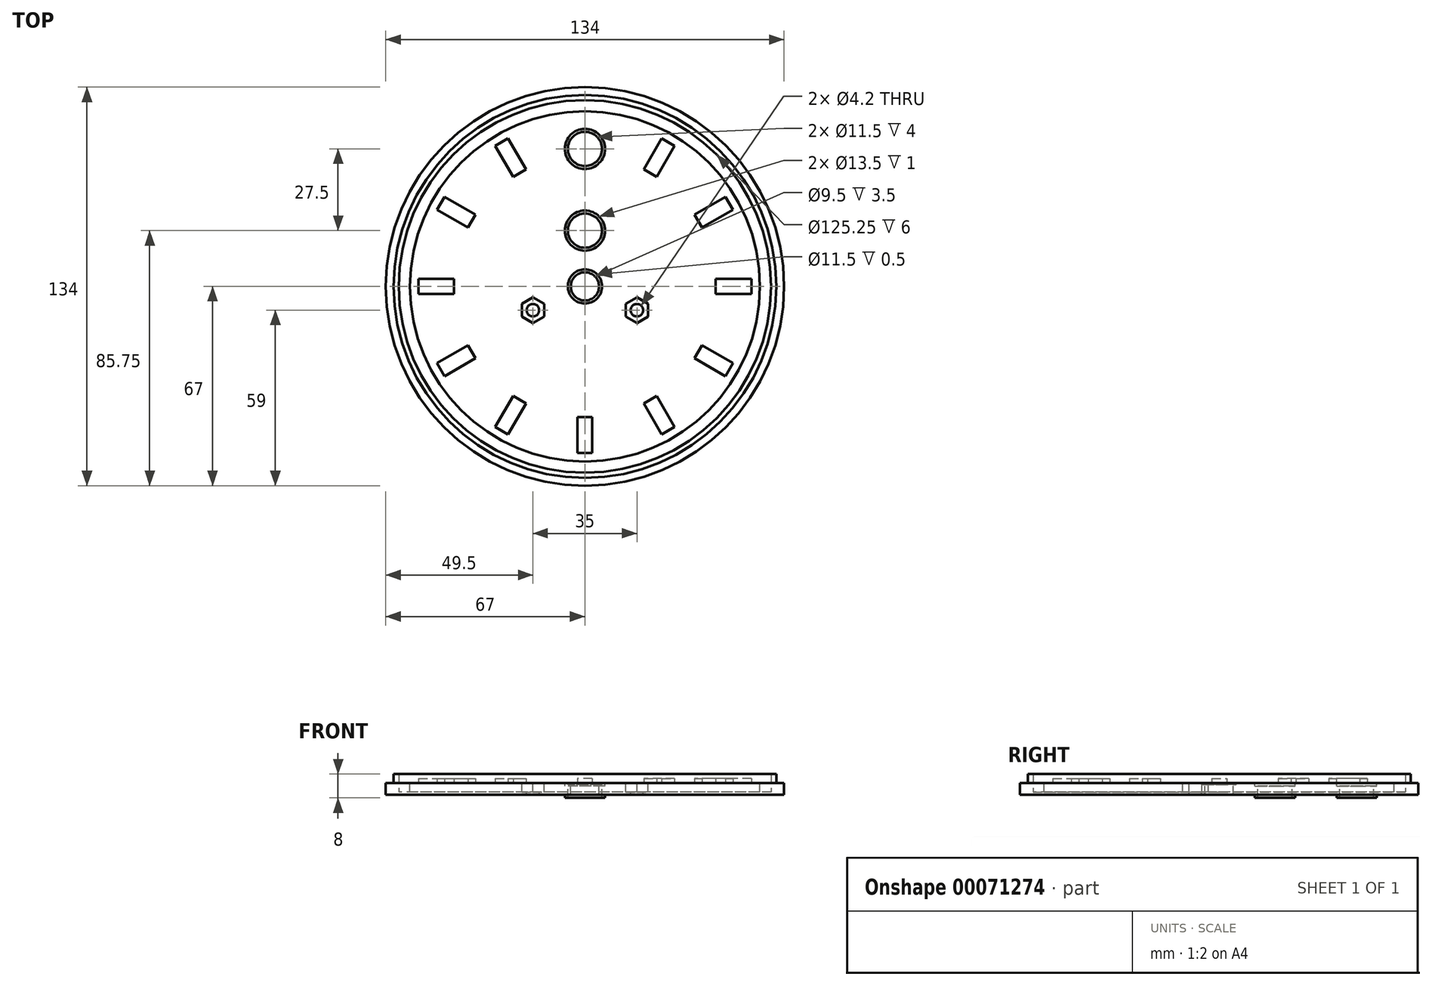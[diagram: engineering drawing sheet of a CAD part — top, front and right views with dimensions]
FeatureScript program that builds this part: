
annotation { "Feature Type Name" : "Feature", "Feature Type Description" : "" }
export const myFeature = defineFeature(function(context is Context, id is Id, definition is map)
    precondition{}
    {
        {
            var Q0;
            Q0=qCreatedBy(makeId("Top.planeOp"),FACE);
            var sketch = newSketch(context, id + "F0", { "sketchPlane" : qUnion([Q0])});
            skCircle(sketch, "E0", {"center": v(0, 0) * mm, "radius": 67 * mm});
            skSolve(sketch);
        }
        {
            var Q0;
            Q0=makeQuery(id+"F0.imprint","IMPRINT",FACE,{"disambiguationData":[TD([[makeQuery(id+"F0.imprint","IMPRINT",EDGE,{"derivedFrom":sQuery(id+"F0.wireOp",EDGE,"E0")}),1.0]])]});
            extrude(context, id + "F1", {"entities" : qUnion([Q0]), "endBound" : BoundingType.SYMMETRIC, "depth" : 5 * mm});
        }
        {
            var Q0;
            Q0=makeQuery(id+"F1.opExtrude","CAP_FACE",FACE,{"disambiguationData":[OSD([sQuery(id+"F0.wireOp",EDGE,"E0")])],"isStart":false});
            var sketch = newSketch(context, id + "F2", { "sketchPlane" : qUnion([Q0])});
            skCircle(sketch, "E1", {"center": v(0, 0) * mm, "radius": 64.38 * mm});
            skCircle(sketch, "E2", {"center": v(0, 0) * mm, "radius": 62.62 * mm});
            skCircle(sketch, "E3", {"center": v(0, 0) * mm, "radius": 58.88 * mm});
            skSolve(sketch);
        }
        {
            var Q0;
            Q0=makeQuery(id+"F2.imprint","IMPRINT",FACE,{"disambiguationData":[TD([[makeQuery(id+"F2.imprint","IMPRINT",EDGE,{"derivedFrom":sQuery(id+"F2.wireOp",EDGE,"E1")}),1.0]])]});
            extrude(context, id + "F3", {"entities" : qUnion([Q0]), "operationType" : NewBodyOperationType.ADD, "depth" : 3 * mm});
        }
        {
            var Q0;
            Q0=makeQuery(id+"F2.imprint","IMPRINT",FACE,{"disambiguationData":[TD([[makeQuery(id+"F2.imprint","IMPRINT",EDGE,{"derivedFrom":sQuery(id+"F2.wireOp",EDGE,"E3")}),1.0]])]});
            var sketch = newSketch(context, id + "F4", { "sketchPlane" : qUnion([Q0])});
            skCircle(sketch, "E4", {"center": v(0, 0) * mm, "radius": 4.75 * mm});
            skCircle(sketch, "E5", {"center": v(0, 18.75) * mm, "radius": 5.75 * mm});
            skCircle(sketch, "E6", {"center": v(0, 46.25) * mm, "radius": 5.75 * mm});
            skCircle(sketch, "E7", {"center": v(17.5, -8) * mm, "radius": 2.1 * mm});
            skCircle(sketch, "E8.MirrorC", {"center": v(-17.5, -8) * mm, "radius": 2.1 * mm});
            skSolve(sketch);
        }
        {
            var Q0;
            Q0 = qSketchRegion(id + "F4", true);
            extrude(context, id + "F5", {"entities" : qUnion([Q0]), "operationType" : NewBodyOperationType.REMOVE, "endBound" : BoundingType.THROUGH_ALL, "oppositeDirection" : true, "depth" : 25 * mm});
        }
        {
            var Q0;
            Q0=makeQuery(id+"F2.imprint","IMPRINT",FACE,{"disambiguationData":[TD([[makeQuery(id+"F2.imprint","IMPRINT",EDGE,{"derivedFrom":sQuery(id+"F2.wireOp",EDGE,"E3")}),1.0]])]});
            var sketch = newSketch(context, id + "F6", { "sketchPlane" : qUnion([Q0])});
            skCircle(sketch, "E9.0", {"center": v(0, 46.25) * mm, "radius": 6.75 * mm});
            skCircle(sketch, "E10.0", {"center": v(0, 18.75) * mm, "radius": 6.75 * mm});
            skCircle(sketch, "E11.0", {"center": v(0, 0) * mm, "radius": 5.75 * mm});
            skCircle(sketch, "E12.cCircle", {"center": v(-17.5, -8) * mm, "radius": 3.75 * mm, "construction": true});
            skLineSegment(sketch, "E12.0", {"start": v(-13.75, -5.83) * mm, "end": v(-13.75, -10.17) * mm});
            skLineSegment(sketch, "E12.1", {"start": v(-13.75, -10.17) * mm, "end": v(-17.5, -12.33) * mm});
            skLineSegment(sketch, "E12.2", {"start": v(-17.5, -12.33) * mm, "end": v(-21.25, -10.17) * mm});
            skLineSegment(sketch, "E12.3", {"start": v(-21.25, -10.17) * mm, "end": v(-21.25, -5.83) * mm});
            skLineSegment(sketch, "E12.4", {"start": v(-21.25, -5.83) * mm, "end": v(-17.5, -3.67) * mm});
            skLineSegment(sketch, "E12.5", {"start": v(-17.5, -3.67) * mm, "end": v(-13.75, -5.83) * mm});
            skPoint(sketch, "E12.0.midPoint", {"position": v(-13.75, -8) * mm});
            skCircle(sketch, "E13.cCircle", {"center": v(17.5, -8) * mm, "radius": 3.75 * mm, "construction": true});
            skLineSegment(sketch, "E13.0", {"start": v(21.25, -5.83) * mm, "end": v(21.25, -10.17) * mm});
            skLineSegment(sketch, "E13.1", {"start": v(21.25, -10.17) * mm, "end": v(17.5, -12.33) * mm});
            skLineSegment(sketch, "E13.2", {"start": v(17.5, -12.33) * mm, "end": v(13.75, -10.17) * mm});
            skLineSegment(sketch, "E13.3", {"start": v(13.75, -10.17) * mm, "end": v(13.75, -5.83) * mm});
            skLineSegment(sketch, "E13.4", {"start": v(13.75, -5.83) * mm, "end": v(17.5, -3.67) * mm});
            skLineSegment(sketch, "E13.5", {"start": v(17.5, -3.67) * mm, "end": v(21.25, -5.83) * mm});
            skPoint(sketch, "E13.0.midPoint", {"position": v(21.25, -8) * mm});
            skSolve(sketch);
        }
        {
            var Q0;
            Q0=makeQuery(id+"F6.imprint","IMPRINT",FACE,{"disambiguationData":[TD([[makeQuery(id+"F6.imprint","IMPRINT",EDGE,{"derivedFrom":sQuery(id+"F6.wireOp",EDGE,"E11.0")}),1.0]])]});
            extrude(context, id + "F7", {"entities" : qUnion([Q0]), "operationType" : NewBodyOperationType.REMOVE, "oppositeDirection" : true, "depth" : .5 * mm});
        }
        {
            var Q0;
            Q0=makeQuery(id+"F6.imprint","IMPRINT",FACE,{"disambiguationData":[TD([[makeQuery(id+"F6.imprint","IMPRINT",EDGE,{"derivedFrom":sQuery(id+"F6.wireOp",EDGE,"E10.0")}),1.0]])]});
            var Q1;
            Q1=makeQuery(id+"F6.imprint","IMPRINT",FACE,{"disambiguationData":[TD([[makeQuery(id+"F6.imprint","IMPRINT",EDGE,{"derivedFrom":sQuery(id+"F6.wireOp",EDGE,"E9.0")}),1.0]])]});
            extrude(context, id + "F8", {"entities" : qUnion([Q0, Q1]), "operationType" : NewBodyOperationType.REMOVE, "oppositeDirection" : true, "depth" : 1 * mm});
        }
        {
            var Q0;
            Q0=makeQuery(id+"F2.imprint","IMPRINT",FACE,{"disambiguationData":[TD([[makeQuery(id+"F2.imprint","IMPRINT",EDGE,{"derivedFrom":sQuery(id+"F2.wireOp",EDGE,"E2")}),1.0]])]});
            extrude(context, id + "F9", {"entities" : qUnion([Q0]), "operationType" : NewBodyOperationType.REMOVE, "oppositeDirection" : true, "depth" : 3 * mm});
        }
        {
            var Q0;
            Q0=makeQuery(id+"F1.opExtrude","CAP_FACE",FACE,{"disambiguationData":[OSD([sQuery(id+"F0.wireOp",EDGE,"E0")])],"isStart":true});
            var sketch = newSketch(context, id + "F10", { "sketchPlane" : qUnion([Q0])});
            skCircle(sketch, "E14.0", {"center": v(0, -18.75) * mm, "radius": 6.75 * mm});
            skCircle(sketch, "E14.1", {"center": v(0, -46.25) * mm, "radius": 6.75 * mm});
            skSolve(sketch);
        }
        {
            var Q0;
            Q0=makeQuery(id+"F10.imprint","IMPRINT",FACE,{"disambiguationData":[TD([[makeQuery(id+"F10.imprint","IMPRINT",EDGE,{"derivedFrom":sQuery(id+"F10.wireOp",EDGE,"E14.0")}),-1.0]])]});
            var Q1;
            Q1=makeQuery(id+"F10.imprint","IMPRINT",FACE,{"disambiguationData":[TD([[makeQuery(id+"F10.imprint","IMPRINT",EDGE,{"derivedFrom":sQuery(id+"F10.wireOp",EDGE,"E14.1")}),-1.0]])]});
            extrude(context, id + "F11", {"entities" : qUnion([Q0, Q1]), "operationType" : NewBodyOperationType.REMOVE, "oppositeDirection" : true, "depth" : 1 * mm});
        }
        {
            var Q0;
            Q0=makeQuery(id+"F2.imprint","IMPRINT",FACE,{"disambiguationData":[TD([[makeQuery(id+"F2.imprint","IMPRINT",EDGE,{"derivedFrom":sQuery(id+"F2.wireOp",EDGE,"E3")}),1.0]])]});
            var sketch = newSketch(context, id + "F12", { "sketchPlane" : qUnion([Q0])});
            skCircle(sketch, "E15", {"center": v(0, 0) * mm, "radius": 50 * mm, "construction": true});
            skSolve(sketch);
        }
        {
            var Q0;
            Q0=makeQuery(id+"F2.imprint","IMPRINT",FACE,{"disambiguationData":[TD([[makeQuery(id+"F2.imprint","IMPRINT",EDGE,{"derivedFrom":sQuery(id+"F2.wireOp",EDGE,"E3")}),1.0]])]});
            var sketch = newSketch(context, id + "F13", { "sketchPlane" : qUnion([Q0])});
            skLineSegment(sketch, "E16.rect.bottom", {"start": v(2.5, -56) * mm, "end": v(-2.5, -56) * mm});
            skLineSegment(sketch, "E16.rect.top", {"start": v(2.5, -44) * mm, "end": v(-2.5, -44) * mm});
            skLineSegment(sketch, "E16.rect.left", {"start": v(2.5, -56) * mm, "end": v(2.5, -44) * mm});
            skLineSegment(sketch, "E16.rect.right", {"start": v(-2.5, -56) * mm, "end": v(-2.5, -44) * mm});
            skPoint(sketch, "E16.rect.middle", {"position": v(0, -50) * mm});
            skSolve(sketch);
        }
        {
            var Q0;
            Q0 = qSketchRegion(id + "F13", true);
            extrude(context, id + "F14", {"entities" : qUnion([Q0]), "operationType" : NewBodyOperationType.ADD, "depth" : 1.5 * mm});
        }
        {
            var Q0;
            Q0=makeQuery(id+"F14.opExtrude","CAP_FACE",FACE,{"disambiguationData":[OSD([sQuery(id+"F13.wireOp",EDGE,"E16.rect.bottom"),sQuery(id+"F13.wireOp",EDGE,"E16.rect.top"),sQuery(id+"F13.wireOp",EDGE,"E16.rect.left"),sQuery(id+"F13.wireOp",EDGE,"E16.rect.right")])],"isStart":false});
            var Q1;
            Q1=makeQuery(id+"F14.opExtrude","SWEPT_FACE",FACE,{"disambiguationData":[OSD([sQuery(id+"F13.wireOp",EDGE,"E16.rect.bottom")])]});
            var Q2;
            Q2=makeQuery(id+"F14.opExtrude","SWEPT_FACE",FACE,{"disambiguationData":[OSD([sQuery(id+"F13.wireOp",EDGE,"E16.rect.left")])]});
            var Q3;
            Q3=makeQuery(id+"F14.opExtrude","SWEPT_FACE",FACE,{"disambiguationData":[OSD([sQuery(id+"F13.wireOp",EDGE,"E16.rect.right")])]});
            var Q4;
            Q4=makeQuery(id+"F14.opExtrude","SWEPT_FACE",FACE,{"disambiguationData":[OSD([sQuery(id+"F13.wireOp",EDGE,"E16.rect.top")])]});
            var Q5;
            Q5=sQuery(id+"F2.wireOp",EDGE,"E3");
            circularPattern(context, id + "F15", {"faces" : qUnion([Q0, Q1, Q2, Q3, Q4]), "axis" : qUnion([Q5]), "angle" : 30 * degree, "instanceCount" : 6, "patternType" : PatternType.FACE});
        }
        {
            var Q0;
            Q0=makeQuery(id+"F14.opExtrude","CAP_FACE",FACE,{"disambiguationData":[OSD([sQuery(id+"F13.wireOp",EDGE,"E16.rect.bottom"),sQuery(id+"F13.wireOp",EDGE,"E16.rect.top"),sQuery(id+"F13.wireOp",EDGE,"E16.rect.left"),sQuery(id+"F13.wireOp",EDGE,"E16.rect.right")])],"isStart":false});
            var Q1;
            Q1=makeQuery(id+"F14.opExtrude","SWEPT_FACE",FACE,{"disambiguationData":[OSD([sQuery(id+"F13.wireOp",EDGE,"E16.rect.right")])]});
            var Q2;
            Q2=makeQuery(id+"F14.opExtrude","SWEPT_FACE",FACE,{"disambiguationData":[OSD([sQuery(id+"F13.wireOp",EDGE,"E16.rect.bottom")])]});
            var Q3;
            Q3=makeQuery(id+"F14.opExtrude","SWEPT_FACE",FACE,{"disambiguationData":[OSD([sQuery(id+"F13.wireOp",EDGE,"E16.rect.left")])]});
            var Q4;
            Q4=makeQuery(id+"F14.opExtrude","SWEPT_FACE",FACE,{"disambiguationData":[OSD([sQuery(id+"F13.wireOp",EDGE,"E16.rect.top")])]});
            var Q5;
            Q5=sQuery(id+"F2.wireOp",EDGE,"E3");
            circularPattern(context, id + "F16", {"operationType" : NewBodyOperationType.ADD, "faces" : qUnion([Q0, Q1, Q2, Q3, Q4]), "axis" : qUnion([Q5]), "angle" : 30 * degree, "instanceCount" : 6, "oppositeDirection" : true, "patternType" : PatternType.FACE});
        }
        {
            var Q0;
            Q0=makeQuery(id+"F6.imprint","IMPRINT",FACE,{"disambiguationData":[TD([[makeQuery(id+"F6.imprint","IMPRINT",EDGE,{"derivedFrom":sQuery(id+"F6.wireOp",EDGE,"E12.0")}),-1.0]])]});
            var Q1;
            Q1=makeQuery(id+"F6.imprint","IMPRINT",FACE,{"disambiguationData":[TD([[makeQuery(id+"F6.imprint","IMPRINT",EDGE,{"derivedFrom":sQuery(id+"F6.wireOp",EDGE,"E13.0")}),-1.0]])]});
            extrude(context, id + "F17", {"entities" : qUnion([Q0, Q1]), "operationType" : NewBodyOperationType.REMOVE, "oppositeDirection" : true, "depth" : 3 * mm});
        }
    });
